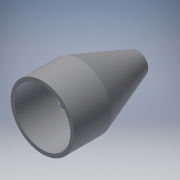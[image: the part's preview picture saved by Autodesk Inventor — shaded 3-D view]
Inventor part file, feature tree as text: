
AUTODESK INVENTOR PART (.ipt)
format: ipt  version: 2016 (Build 200138000, 138)  size: 118,784 bytes
history: native  units: mm
features: extrude x3, sketch x2, plane x1
ambient origin geometry x8: Origin, YZ Plane, XZ Plane, XY Plane, X Axis, Y Axis, Z Axis, Center Point
bodies: Body1 (feature_tree)
feature tree (6):
  plane  "Work Plane1"
  extrude  "Extrusion3"  Depth=31.0mm
  extrude  "Extrusion6"  Depth=30.0mm
  extrude  "Extrusion7"  Depth=30.0mm
  sketch  "Sketch5"  dims[d8=34.0mm d9=31.0mm d10=-3.490659mm]
  sketch  "Sketch7"  dims[d11=30.0mm d14=30.0mm d15=34.0mm d19=20.0mm d20=0.0mm d22=40.0mm d23=-3.490659mm]
